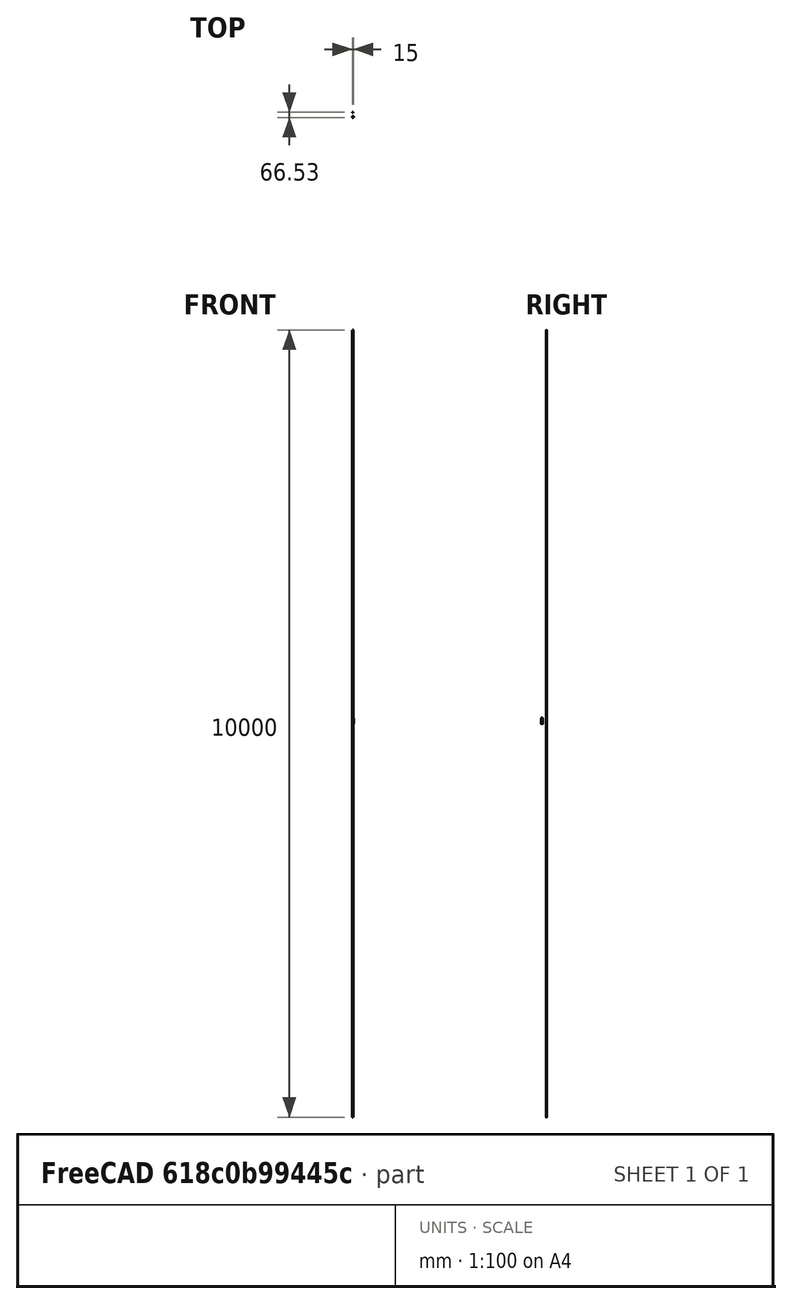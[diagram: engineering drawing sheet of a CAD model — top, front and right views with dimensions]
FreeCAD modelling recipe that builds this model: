
FCSTD DOCUMENT  (FreeCAD 0.16R6707 (Git))
Label: falcon9-7
License: All rights reserved
LicenseURL: http://en.wikipedia.org/wiki/All_rights_reserved
objects: Part::Sphere×9, Part::Cylinder×6, Part::Cone×6, PartDesign::Pocket×1, Sketcher::SketchObject×1
note: 24 computed .brp shape members not serialized (recipe doc carries the construction recipe); baked Part::Feature solids carry a one-line shape summary decoded from their .brp

FEATURE [Part::Cylinder] Cylinder005  label="Cylindre005"
  Angle = 360
  Height = 15
  Placement = pos=(0,0,47) rot=(0,0,1;0rad)
  Radius = 6
FEATURE [Part::Cylinder] Cylinder  label="Cylindre"
  Angle = 360
  Height = 41
  Radius = 5
FEATURE [Part::Cone] Cone  label="Cône"
  Angle = 360
  Height = 10
  Placement = pos=(0,0,62) rot=(0,0,1;0rad)
  Radius1 = 6
  Radius2 = 2
FEATURE [Part::Cylinder] Cylinder001  label="Cylindre001"
  Angle = 360
  Height = 30
  Placement = pos=(5,0,0) rot=(0,0,1;0rad)
  Radius = 2.5
FEATURE [Part::Cylinder] Cylinder002  label="Cylindre002"
  Angle = 360
  Height = 30
  Placement = pos=(-5,0,0) rot=(0,0,1;0rad)
  Radius = 2.5
FEATURE [Part::Cylinder] Cylinder003  label="Cylindre003"
  Angle = 360
  Height = 30
  Placement = pos=(0,5,0) rot=(0,0,1;0rad)
  Radius = 2.5
FEATURE [Part::Cylinder] Cylinder004  label="Cylindre004"
  Angle = 360
  Height = 30
  Placement = pos=(0,-5,0) rot=(0,0,1;0rad)
  Radius = 2.5
FEATURE [Part::Cone] Cone001  label="Cône001"
  Angle = 360
  Height = 6
  Placement = pos=(0,0,41) rot=(0,0,1;0rad)
  Radius1 = 5
  Radius2 = 6
FEATURE [Part::Sphere] Sphere  label="Sphère"
  Angle1 = -90
  Angle2 = 90
  Angle3 = 360
  Placement = pos=(0,0,72) rot=(0,0,1;0rad)
  Radius = 1.9
FEATURE [PartDesign::Pocket] Pocket
  Length = 5
  Midplane = true
  Placement = pos=(0,0,0) rot=(1,0,0;1.5708rad)
  Type = 1
FEATURE [Part::Sphere] Sphere001  label="Sphère001"
  Angle1 = -90
  Angle2 = 90
  Angle3 = 360
  Placement = pos=(5,0,30) rot=(0,0,1;0rad)
  Radius = 2.5
FEATURE [Part::Sphere] Sphere002  label="Sphère002"
  Angle1 = -90
  Angle2 = 90
  Angle3 = 360
  Placement = pos=(-5,0,30) rot=(0,0,1;0rad)
  Radius = 2.5
FEATURE [Part::Sphere] Sphere003  label="Sphère003"
  Angle1 = -90
  Angle2 = 90
  Angle3 = 360
  Placement = pos=(0,5,30) rot=(0,0,1;0rad)
  Radius = 2.5
FEATURE [Part::Sphere] Sphere004  label="Sphère004"
  Angle1 = -90
  Angle2 = 90
  Angle3 = 360
  Placement = pos=(0,-5,30) rot=(0,0,1;0rad)
  Radius = 2.5
FEATURE [Sketcher::SketchObject] Sketch
  Placement = pos=(0,0,10) rot=(0,0,1;0rad)
FEATURE [Part::Cone] Cone002  label="Cône002"
  Angle = 360
  Height = 7
  Placement = pos=(5,0,30) rot=(0,0,1;0rad)
  Radius1 = 2.5
  Radius2 = 0.5
FEATURE [Part::Cone] Cone003  label="Cône003"
  Angle = 360
  Height = 7
  Placement = pos=(-5,0,30) rot=(0,0,1;0rad)
  Radius1 = 2.5
  Radius2 = 0.5
FEATURE [Part::Cone] Cone004  label="Cône004"
  Angle = 360
  Height = 7
  Placement = pos=(0,5,30) rot=(0,0,1;0rad)
  Radius1 = 2.5
  Radius2 = 0.5
FEATURE [Part::Cone] Cone005  label="Cône005"
  Angle = 360
  Height = 7
  Placement = pos=(0,-5,30) rot=(0,0,1;0rad)
  Radius1 = 2.5
  Radius2 = 0.5
FEATURE [Part::Sphere] Sphere005  label="Sphère005"
  Angle1 = -90
  Angle2 = 90
  Angle3 = 360
  Placement = pos=(5,0,37) rot=(0,0,1;0rad)
  Radius = 0.5
FEATURE [Part::Sphere] Sphere006  label="Sphère006"
  Angle1 = -90
  Angle2 = 90
  Angle3 = 360
  Placement = pos=(-5,0,37) rot=(0,0,1;0rad)
  Radius = 0.5
FEATURE [Part::Sphere] Sphere007  label="Sphère007"
  Angle1 = -90
  Angle2 = 90
  Angle3 = 360
  Placement = pos=(0,5,37) rot=(0,0,1;0rad)
  Radius = 0.5
FEATURE [Part::Sphere] Sphere008  label="Sphère008"
  Angle1 = -90
  Angle2 = 90
  Angle3 = 360
  Placement = pos=(0,-5,37) rot=(0,0,1;0rad)
  Radius = 0.5
